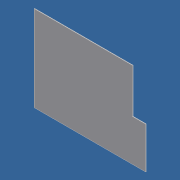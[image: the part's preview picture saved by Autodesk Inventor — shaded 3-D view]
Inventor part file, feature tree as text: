
AUTODESK INVENTOR PART (.ipt)
format: ipt  version: 2012 (Build 160160000, 160)  size: 68,608 bytes
history: native  units: in
note: dims shown in document units (in); Inventor stores cm internally (conversion verified against a paired STEP export)
features: extrude x1, sketch x1
ambient origin geometry x8: Origin, YZ Plane, XZ Plane, XY Plane, X Axis, Y Axis, Z Axis, Center Point
bodies: Solid1 (feature_tree)
feature tree (2):
  extrude  "Extrusion1"  Depth=38.75in
  sketch  "Sketch1"  dims[d0=50.5in d1=38.75in d2=44.5in d3=20.0in d4=0.25in d5=0.0in]
